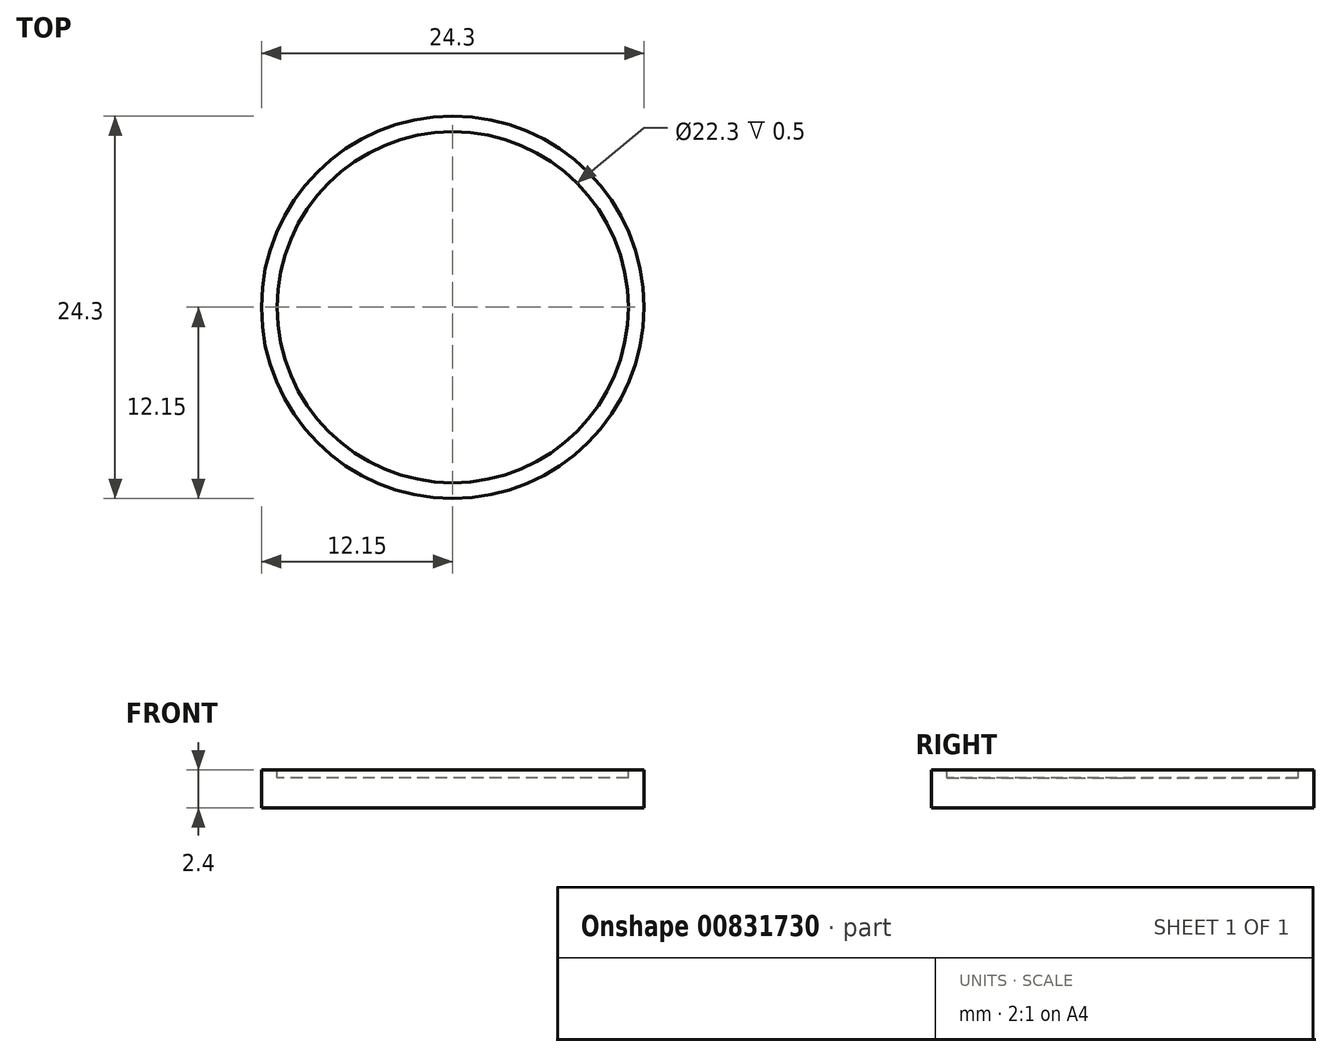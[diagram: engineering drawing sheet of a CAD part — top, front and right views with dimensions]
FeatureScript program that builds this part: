
annotation { "Feature Type Name" : "Feature", "Feature Type Description" : "" }
export const myFeature = defineFeature(function(context is Context, id is Id, definition is map)
    precondition{}
    {
        {
            var Q0;
            Q0=qCreatedBy(makeId("Top.planeOp"),FACE);
            var sketch = newSketch(context, id + "F0", { "sketchPlane" : qUnion([Q0])});
            skCircle(sketch, "E0", {"center": v(0, 0) * mm, "radius": 12.15 * mm});
            skSolve(sketch);
        }
        {
            var Q0;
            Q0=makeQuery(id+"F0.imprint","IMPRINT",FACE,{"disambiguationData":[TD([[makeQuery(id+"F0.imprint","IMPRINT",EDGE,{"derivedFrom":sQuery(id+"F0.wireOp",EDGE,"E0")}),1.0]])]});
            extrude(context, id + "F1", {"entities" : qUnion([Q0]), "depth" : 2.4 * mm, "offsetDistance" : 25 * mm});
        }
        {
            var Q0;
            Q0=makeQuery(id+"F1.opExtrude","CAP_FACE",FACE,{"disambiguationData":[OSD([sQuery(id+"F0.wireOp",EDGE,"E0")])],"isStart":false});
            var sketch = newSketch(context, id + "F2", { "sketchPlane" : qUnion([Q0])});
            skCircle(sketch, "E1", {"center": v(0, 0) * mm, "radius": 11.15 * mm});
            skSolve(sketch);
        }
        {
            var Q0;
            Q0=makeQuery(id+"F2.imprint","IMPRINT",FACE,{"disambiguationData":[TD([[makeQuery(id+"F2.imprint","IMPRINT",EDGE,{"derivedFrom":sQuery(id+"F2.wireOp",EDGE,"E1")}),1.0]])]});
            extrude(context, id + "F3", {"entities" : qUnion([Q0]), "operationType" : NewBodyOperationType.REMOVE, "oppositeDirection" : true, "depth" : .5 * mm, "offsetDistance" : 25 * mm});
        }
    });
